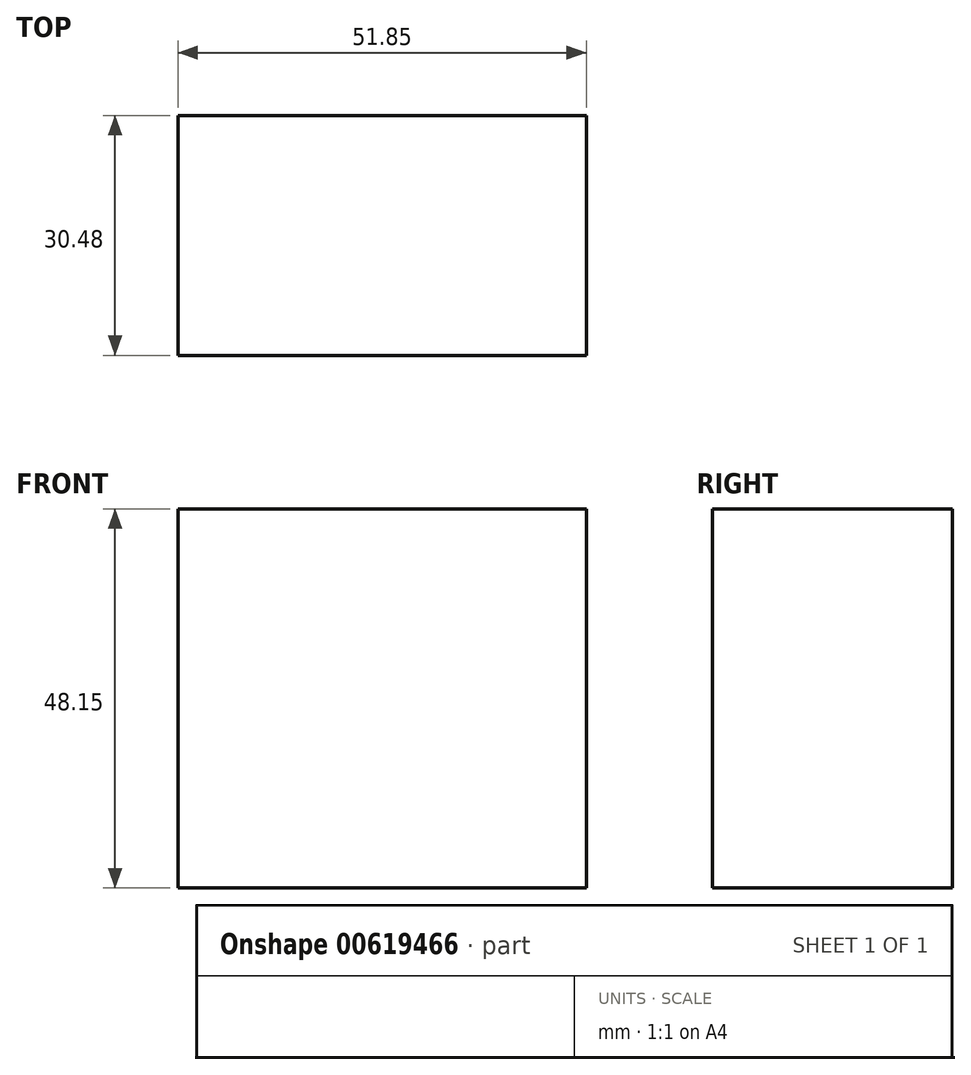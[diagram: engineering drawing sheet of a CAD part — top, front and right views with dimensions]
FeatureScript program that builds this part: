
annotation { "Feature Type Name" : "Feature", "Feature Type Description" : "" }
export const myFeature = defineFeature(function(context is Context, id is Id, definition is map)
    precondition{}
    {
        {
            var Q0;
            Q0=qCreatedBy(makeId("Front.planeOp"),FACE);
            var sketch = newSketch(context, id + "F0", { "sketchPlane" : qUnion([Q0])});
            skLineSegment(sketch, "E0.bottom", {"start": v(-34.04, 83.75) * mm, "end": v(17.81, 83.75) * mm});
            skLineSegment(sketch, "E0.top", {"start": v(-34.04, 35.6) * mm, "end": v(17.81, 35.6) * mm});
            skLineSegment(sketch, "E0.left", {"start": v(-34.04, 83.75) * mm, "end": v(-34.04, 35.6) * mm});
            skLineSegment(sketch, "E0.right", {"start": v(17.81, 83.75) * mm, "end": v(17.81, 35.6) * mm});
            skSolve(sketch);
        }
        {
            var Q0;
            Q0 = qSketchRegion(id + "F0", true);
            extrude(context, id + "F1", {"entities" : qUnion([Q0]), "depth" : 30.48 * mm, "offsetDistance" : 30.48 * mm});
        }
    });
